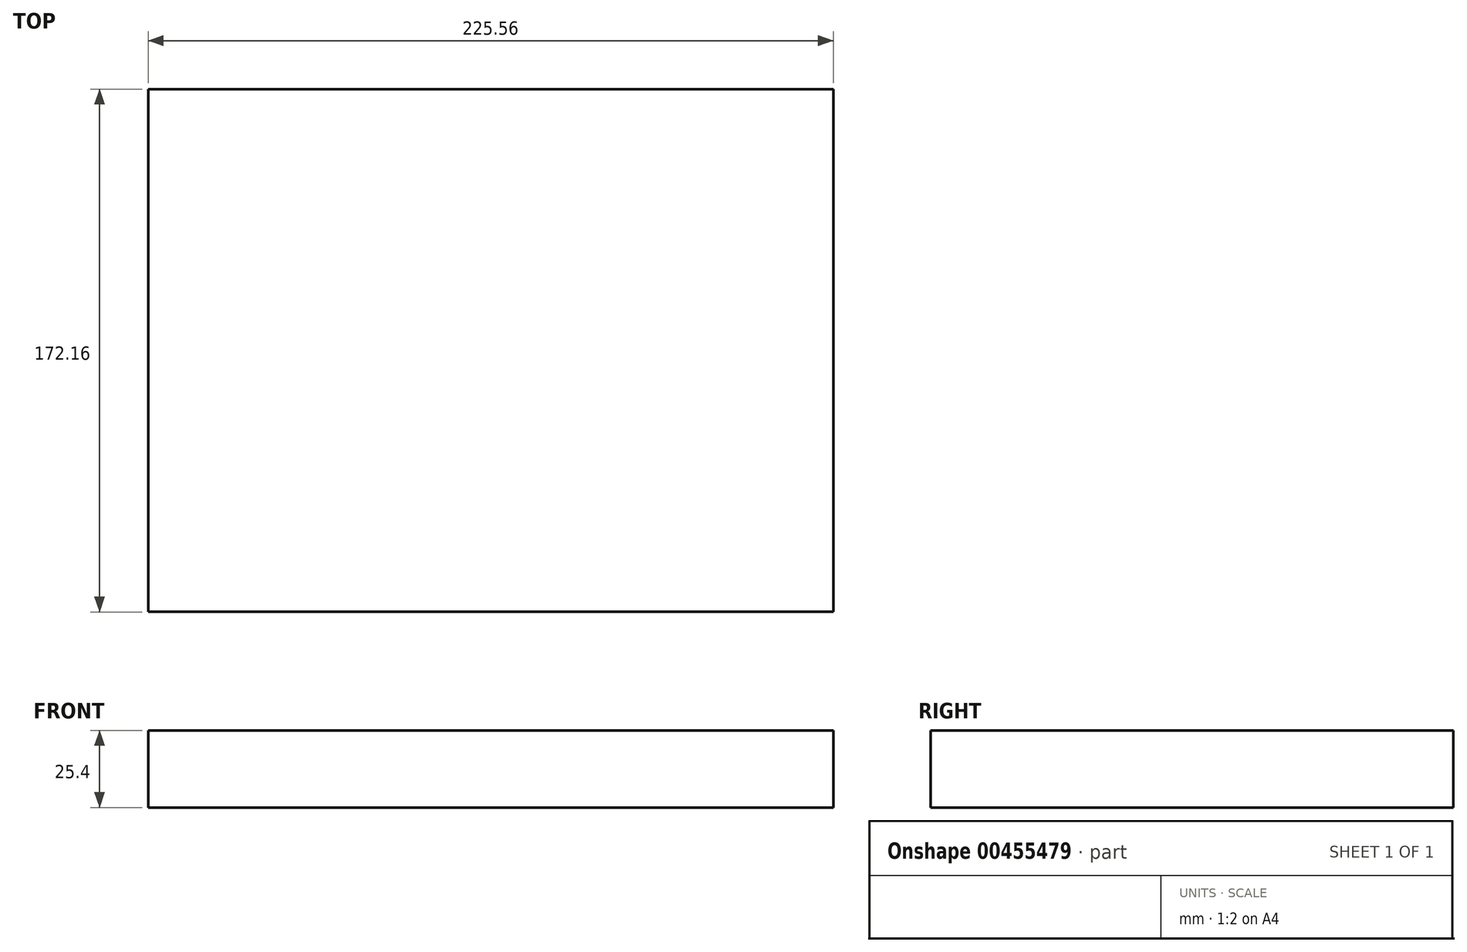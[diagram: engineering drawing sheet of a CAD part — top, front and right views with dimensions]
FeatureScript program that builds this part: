
annotation { "Feature Type Name" : "Feature", "Feature Type Description" : "" }
export const myFeature = defineFeature(function(context is Context, id is Id, definition is map)
    precondition{}
    {
        {
            var Q0;
            Q0=qCreatedBy(makeId("Top.planeOp"),FACE);
            var sketch = newSketch(context, id + "F0", { "sketchPlane" : qUnion([Q0])});
            skLineSegment(sketch, "E0.bottom", {"start": v(-131.4, 42.48) * mm, "end": v(94.16, 42.48) * mm});
            skLineSegment(sketch, "E0.top", {"start": v(-131.4, -129.68) * mm, "end": v(94.16, -129.68) * mm});
            skLineSegment(sketch, "E0.left", {"start": v(-131.4, 42.48) * mm, "end": v(-131.4, -129.68) * mm});
            skLineSegment(sketch, "E0.right", {"start": v(94.16, 42.48) * mm, "end": v(94.16, -129.68) * mm});
            skSolve(sketch);
        }
        {
            var Q0;
            Q0 = qSketchRegion(id + "F0", true);
            extrude(context, id + "F1", {"entities" : qUnion([Q0]), "depth" : 25.4 * mm});
        }
    });
